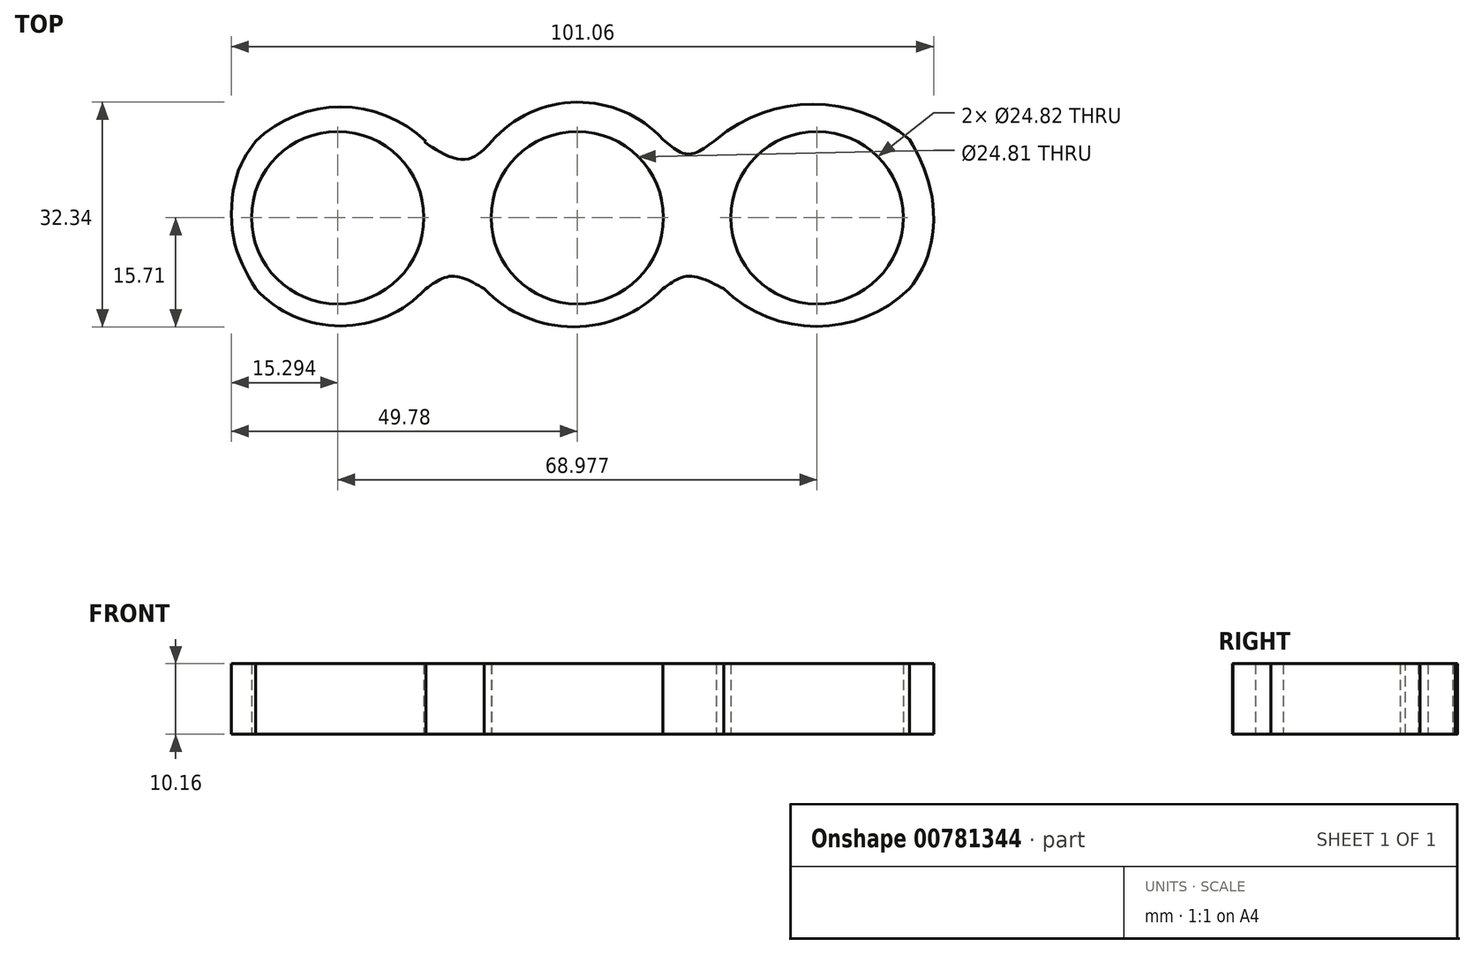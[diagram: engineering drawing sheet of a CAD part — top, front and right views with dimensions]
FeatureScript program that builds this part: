
annotation { "Feature Type Name" : "Feature", "Feature Type Description" : "" }
export const myFeature = defineFeature(function(context is Context, id is Id, definition is map)
    precondition{}
    {
        {
            var Q0;
            Q0=qCreatedBy(makeId("Top.planeOp"),FACE);
            var sketch = newSketch(context, id + "F0", { "sketchPlane" : qUnion([Q0])});
            skCircle(sketch, "E0", {"center": v(0, 0) * mm, "radius": 10.08 * mm});
            skCircle(sketch, "E1", {"center": v(0, 0) * mm, "radius": 12.4 * mm});
            skCircle(sketch, "E2", {"center": v(-34.49, 0) * mm, "radius": 10.08 * mm});
            skCircle(sketch, "E3", {"center": v(34.5, 0) * mm, "radius": 10.08 * mm});
            skCircle(sketch, "E4", {"center": v(-34.49, 0) * mm, "radius": 12.4 * mm});
            skCircle(sketch, "E5", {"center": v(34.5, 0) * mm, "radius": 12.4 * mm});
            skArc(sketch, "E6", {"start": v(12.33, 11.28) * mm, "mid": v(-0.07, 16.62) * mm, "end": v(-12.33, 10.98) * mm});
            skFitSpline(sketch, "E7", {"points": [v(-12.33, 10.98) * mm, v(-17, 8.42) * mm, v(-21.96, 10.98) * mm, v(-21.8, 10.98) * mm], "startDerivative": vector(-8.62, -9.33) * mm, "endDerivative": vector(2.96, -0.65) * mm});
            skArc(sketch, "E8", {"start": v(-21.8, 10.98) * mm, "mid": v(-34.06, 15.94) * mm, "end": v(-46.32, 10.98) * mm});
            skFitSpline(sketch, "E9", {"points": [v(-46.32, 10.98) * mm, v(-48.88, 6.47) * mm, v(-49.48, -2.86) * mm, v(-46.32, -10.23) * mm], "startDerivative": vector(-10.27, -13.95) * mm, "endDerivative": vector(11.33, -19.65) * mm});
            skArc(sketch, "E10", {"start": v(-46.32, -10.23) * mm, "mid": v(-34.06, -15.58) * mm, "end": v(-21.8, -10.23) * mm});
            skFitSpline(sketch, "E11", {"points": [v(-21.8, -10.23) * mm, v(-18.05, -8.42) * mm, v(-13.39, -10.23) * mm], "startDerivative": vector(7.63, 5.5) * mm, "endDerivative": vector(9.2, -5.34) * mm});
            skArc(sketch, "E12", {"start": v(-13.39, -10.23) * mm, "mid": v(-0.53, -15.7) * mm, "end": v(12.33, -10.23) * mm});
            skFitSpline(sketch, "E13", {"points": [v(12.33, -10.23) * mm, v(15.94, -8.42) * mm, v(21.06, -10.23) * mm], "startDerivative": vector(7.4, 5.58) * mm, "endDerivative": vector(9.99, -5.31) * mm});
            skArc(sketch, "E14", {"start": v(21.06, -10.23) * mm, "mid": v(34.44, -15.65) * mm, "end": v(47.83, -10.23) * mm});
            skFitSpline(sketch, "E15", {"points": [v(12.33, 11.28) * mm, v(15.94, 9.17) * mm, v(20, 11.28) * mm], "startDerivative": vector(7.25, -6.37) * mm, "endDerivative": vector(8.08, 6.27) * mm});
            skArc(sketch, "E16", {"start": v(47.83, 11.28) * mm, "mid": v(33.91, 16.32) * mm, "end": v(20, 11.28) * mm});
            skFitSpline(sketch, "E17", {"points": [v(47.83, -10.23) * mm, v(50.08, -6.47) * mm, v(51.28, 0) * mm, v(50.08, 6.62) * mm, v(47.83, 11.28) * mm], "startDerivative": vector(11.18, 15.53) * mm, "endDerivative": vector(-10.21, 18.42) * mm});
            skSolve(sketch);
        }
        {
            var Q0;
            Q0 = qSketchRegion(id + "F0", true);
            extrude(context, id + "F1", {"entities" : qUnion([Q0]), "depth" : 10.16 * mm, "offsetDistance" : 25.4 * mm});
        }
    });
